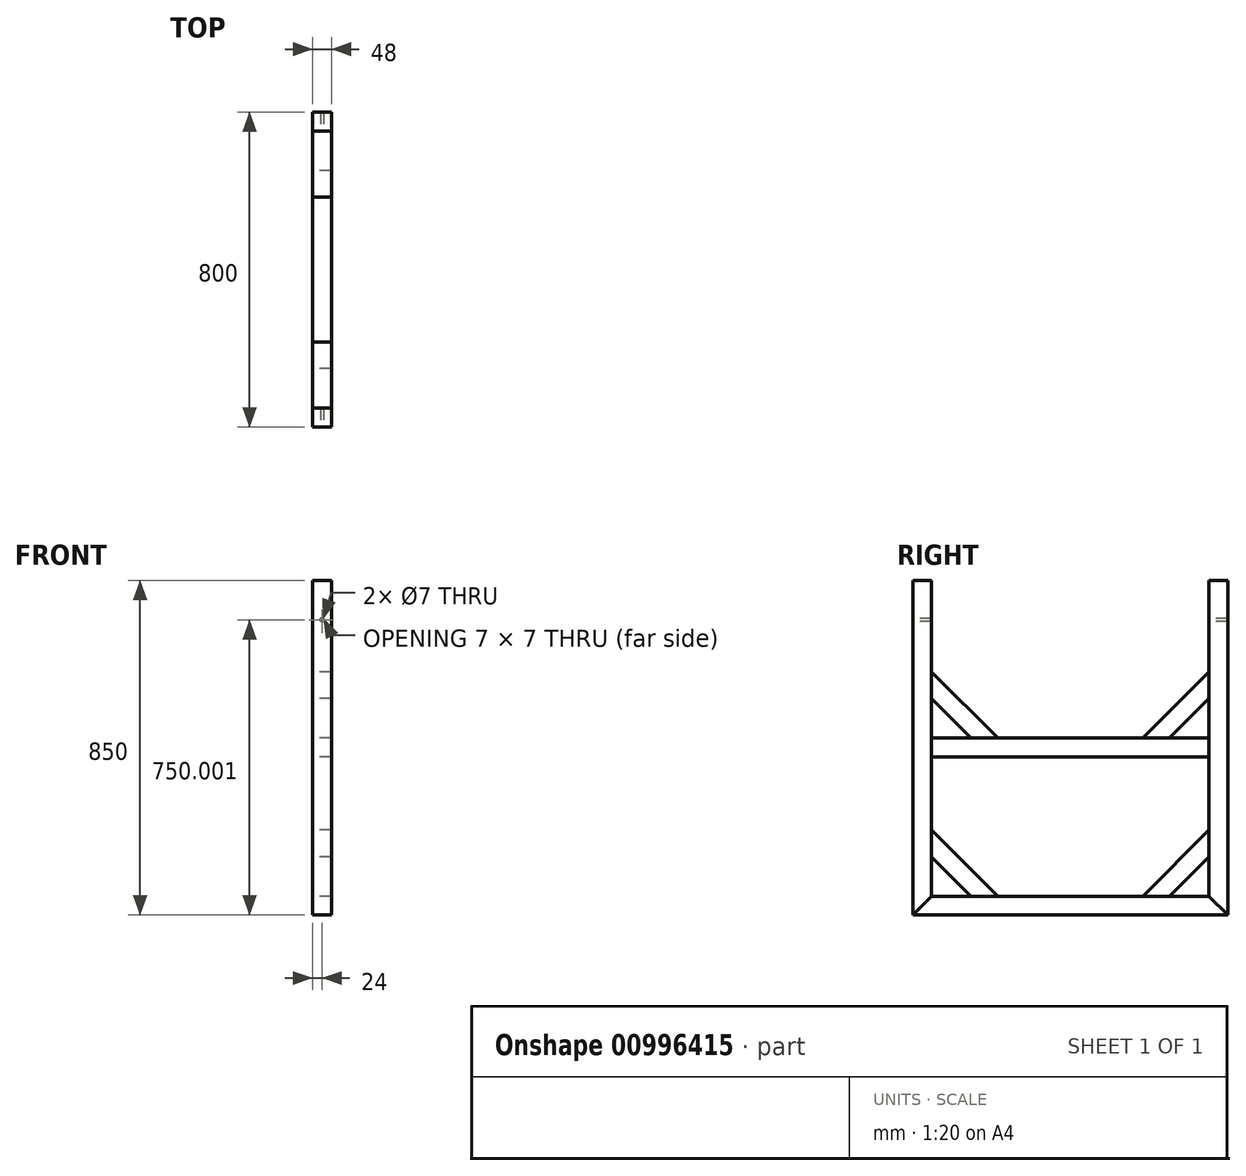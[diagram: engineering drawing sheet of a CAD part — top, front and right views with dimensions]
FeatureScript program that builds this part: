
annotation { "Feature Type Name" : "Feature", "Feature Type Description" : "" }
export const myFeature = defineFeature(function(context is Context, id is Id, definition is map)
    precondition{}
    {
        {
            var Q0;
            Q0=qCreatedBy(makeId("Right.planeOp"),FACE);
            var sketch = newSketch(context, id + "F0", { "sketchPlane" : qUnion([Q0])});
            skLineSegment(sketch, "E0", {"start": v(-214.94, 609.65) * mm, "end": v(-166.94, 609.65) * mm});
            skLineSegment(sketch, "E1", {"start": v(-166.94, 609.65) * mm, "end": v(-166.94, -192.35) * mm});
            skLineSegment(sketch, "E2", {"start": v(-166.94, -192.35) * mm, "end": v(-214.94, -240.35) * mm});
            skLineSegment(sketch, "E3", {"start": v(-214.94, -240.35) * mm, "end": v(-214.94, 609.65) * mm});
            skLineSegment(sketch, "E4", {"start": v(-166.94, -192.35) * mm, "end": v(537.06, -192.35) * mm});
            skLineSegment(sketch, "E5", {"start": v(537.06, -192.35) * mm, "end": v(585.06, -240.35) * mm});
            skLineSegment(sketch, "E6", {"start": v(585.06, -240.35) * mm, "end": v(-214.94, -240.35) * mm});
            skLineSegment(sketch, "E7", {"start": v(537.06, -192.35) * mm, "end": v(537.06, 609.65) * mm});
            skLineSegment(sketch, "E8", {"start": v(537.06, 609.65) * mm, "end": v(585.06, 609.65) * mm});
            skLineSegment(sketch, "E9", {"start": v(585.06, 609.65) * mm, "end": v(585.06, -240.35) * mm});
            skLineSegment(sketch, "E10", {"start": v(-166.94, 209.65) * mm, "end": v(537.06, 209.65) * mm});
            skLineSegment(sketch, "E11", {"start": v(-166.94, 161.65) * mm, "end": v(537.06, 161.65) * mm});
            skLineSegment(sketch, "E12", {"start": v(-166.94, 309.65) * mm, "end": v(-66.94, 209.65) * mm});
            skLineSegment(sketch, "E13", {"start": v(-166.94, 377.53) * mm, "end": v(0.94, 209.65) * mm});
            skLineSegment(sketch, "E14", {"start": v(537.06, 309.65) * mm, "end": v(437.06, 209.65) * mm});
            skLineSegment(sketch, "E15", {"start": v(537.06, 377.53) * mm, "end": v(369.17, 209.65) * mm});
            skLineSegment(sketch, "E16", {"start": v(537.06, -92.35) * mm, "end": v(437.06, -192.35) * mm});
            skLineSegment(sketch, "E17", {"start": v(537.06, -24.47) * mm, "end": v(369.17, -192.35) * mm});
            skLineSegment(sketch, "E18", {"start": v(-166.94, -92.35) * mm, "end": v(-66.94, -192.35) * mm});
            skLineSegment(sketch, "E19", {"start": v(-166.94, -24.47) * mm, "end": v(0.94, -192.35) * mm});
            skSolve(sketch);
        }
        {
            var Q0;
            {var subQ4=sQuery(id+"F0.wireOp",EDGE,"E2");Q0=makeQuery(id+"F0.imprint","IMPRINT",FACE,{"disambiguationData":[TD([[makeQuery(id+"F0.imprint","IMPRINT",EDGE,{"derivedFrom":subQ4}),1.0]])]});}
            extrude(context, id + "F1", {"entities" : qUnion([Q0]), "depth" : 48 * mm, "offsetDistance" : 25 * mm});
        }
        {
            var Q0;
            {var subQ4=sQuery(id+"F0.wireOp",EDGE,"E0");Q0=makeQuery(id+"F0.imprint","IMPRINT",FACE,{"disambiguationData":[TD([[makeQuery(id+"F0.imprint","IMPRINT",EDGE,{"derivedFrom":subQ4}),-1.0]])]});}
            extrude(context, id + "F2", {"entities" : qUnion([Q0]), "depth" : 48 * mm, "offsetDistance" : 25 * mm});
        }
        {
            var Q0;
            {var subQ0=sQuery(id+"F0.wireOp",EDGE,"E18");Q0=makeQuery(id+"F0.imprint","IMPRINT",FACE,{"disambiguationData":[TD([[makeQuery(id+"F0.imprint","IMPRINT",EDGE,{"derivedFrom":subQ0}),1.0]])]});}
            extrude(context, id + "F3", {"entities" : qUnion([Q0]), "depth" : 48 * mm, "offsetDistance" : 25 * mm});
        }
        {
            var Q0;
            {var subQ0=sQuery(id+"F0.wireOp",EDGE,"E12");Q0=makeQuery(id+"F0.imprint","IMPRINT",FACE,{"disambiguationData":[TD([[makeQuery(id+"F0.imprint","IMPRINT",EDGE,{"derivedFrom":subQ0}),1.0]])]});}
            extrude(context, id + "F4", {"entities" : qUnion([Q0]), "depth" : 48 * mm, "offsetDistance" : 25 * mm});
        }
        {
            var Q0;
            {var subQ0=sQuery(id+"F0.wireOp",EDGE,"E14");Q0=makeQuery(id+"F0.imprint","IMPRINT",FACE,{"disambiguationData":[TD([[makeQuery(id+"F0.imprint","IMPRINT",EDGE,{"derivedFrom":subQ0}),-1.0]])]});}
            extrude(context, id + "F5", {"entities" : qUnion([Q0]), "depth" : 48 * mm, "offsetDistance" : 25 * mm});
        }
        {
            var Q0;
            {var subQ0=sQuery(id+"F0.wireOp",EDGE,"E16");Q0=makeQuery(id+"F0.imprint","IMPRINT",FACE,{"disambiguationData":[TD([[makeQuery(id+"F0.imprint","IMPRINT",EDGE,{"derivedFrom":subQ0}),-1.0]])]});}
            extrude(context, id + "F6", {"entities" : qUnion([Q0]), "depth" : 48 * mm, "offsetDistance" : 25 * mm});
        }
        {
            var Q0;
            {var subQ4=sQuery(id+"F0.wireOp",EDGE,"E5");Q0=makeQuery(id+"F0.imprint","IMPRINT",FACE,{"disambiguationData":[TD([[makeQuery(id+"F0.imprint","IMPRINT",EDGE,{"derivedFrom":subQ4}),1.0]])]});}
            extrude(context, id + "F7", {"entities" : qUnion([Q0]), "depth" : 48 * mm, "offsetDistance" : 25 * mm});
        }
        {
            var Q0;
            {var subQ5=sQuery(id+"F0.wireOp",EDGE,"E11");Q0=makeQuery(id+"F0.imprint","IMPRINT",FACE,{"disambiguationData":[TD([[makeQuery(id+"F0.imprint","IMPRINT",EDGE,{"derivedFrom":subQ5}),1.0]])]});}
            extrude(context, id + "F8", {"entities" : qUnion([Q0]), "depth" : 48 * mm, "offsetDistance" : 25 * mm});
        }
        {
            var Q0;
            Q0=makeQuery(id+"F2.opExtrude","SWEPT_FACE",FACE,{"disambiguationData":[OSD([sQuery(id+"F0.wireOp",EDGE,"E3")])]});
            var sketch = newSketch(context, id + "F9", { "sketchPlane" : qUnion([Q0])});
            skLineSegment(sketch, "E20", {"start": v(24, 509.65) * mm, "end": v(48, 509.65) * mm});
            skLineSegment(sketch, "E21", {"start": v(24, 509.65) * mm, "end": v(0, 509.65) * mm});
            skCircle(sketch, "E22", {"center": v(24, 509.65) * mm, "radius": 3.5 * mm});
            skPoint(sketch, "E23.orphan", {"position": v(24, 609.65) * mm});
            skSolve(sketch);
        }
        {
            var Q0;
            Q0 = qSketchRegion(id + "F9", true);
            extrude(context, id + "F10", {"entities" : qUnion([Q0]), "operationType" : NewBodyOperationType.REMOVE, "endBound" : BoundingType.THROUGH_ALL, "oppositeDirection" : true, "depth" : 25 * mm, "offsetDistance" : 25 * mm});
        }
    });
